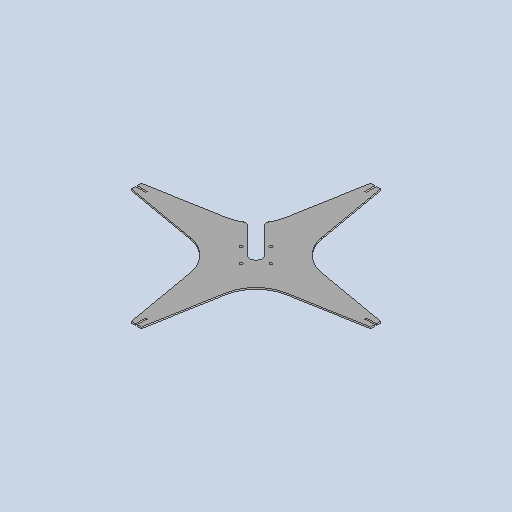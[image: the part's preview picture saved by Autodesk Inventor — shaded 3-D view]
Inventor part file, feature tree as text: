
AUTODESK INVENTOR PART (.ipt)
format: ipt  version: 2025 (Build 290162010, 162A)  size: 366,080 bytes
history: native  units: mm
features: other x6, sketch x4, sheet_metal_op x1, pattern_circular x1, chamfer x1, projected_geometry x1
ambient origin geometry x8: Origin, YZ Plane, XZ Plane, XY Plane, X Axis, Y Axis, Z Axis, Center Point
bodies: Solid1 (feature_tree)
feature tree (14):
  sheet_metal_op  "Face1"
  other  "Mark1"
  other  "A-Side Definition"
  pattern_circular  "Circular Pattern2"  Count=20  [1 undecoded]
  chamfer  "Corner Round1"
  sketch  "Sketch1"  dims[d2=3.0mm d6=200.0mm]
  other  "Plate1"
  sketch  "Sketch2"  dims[d9=20.0mm]
  sketch  "Sketch4"  dims[d15=25.0mm]
  projected_geometry  "Projected Loop2"
  sketch  "Sketch5"  dims[d16=75.0mm d25=480.0mm d28=20.0mm d29=45.0deg d30=1.745329mm d31=75.0mm d32=3.1mm d33=20.0mm d34=3.0mm d35=0.0mm d36=40.0mm d37=360.0deg d39=60.0mm d40=90.0deg d41=6.0mm d42=45.0deg d43=100.0mm d44=3.0mm d45=0.0mm d46=6.0mm]
  other  "Cut2"
  other  "Cut3"
  other  "Definition1"
note: 1 required parameter value undecoded (feature->parameter linkage not recoverable at this tier; creation-order binding heuristic only, values carry confidence <= 0.55)
